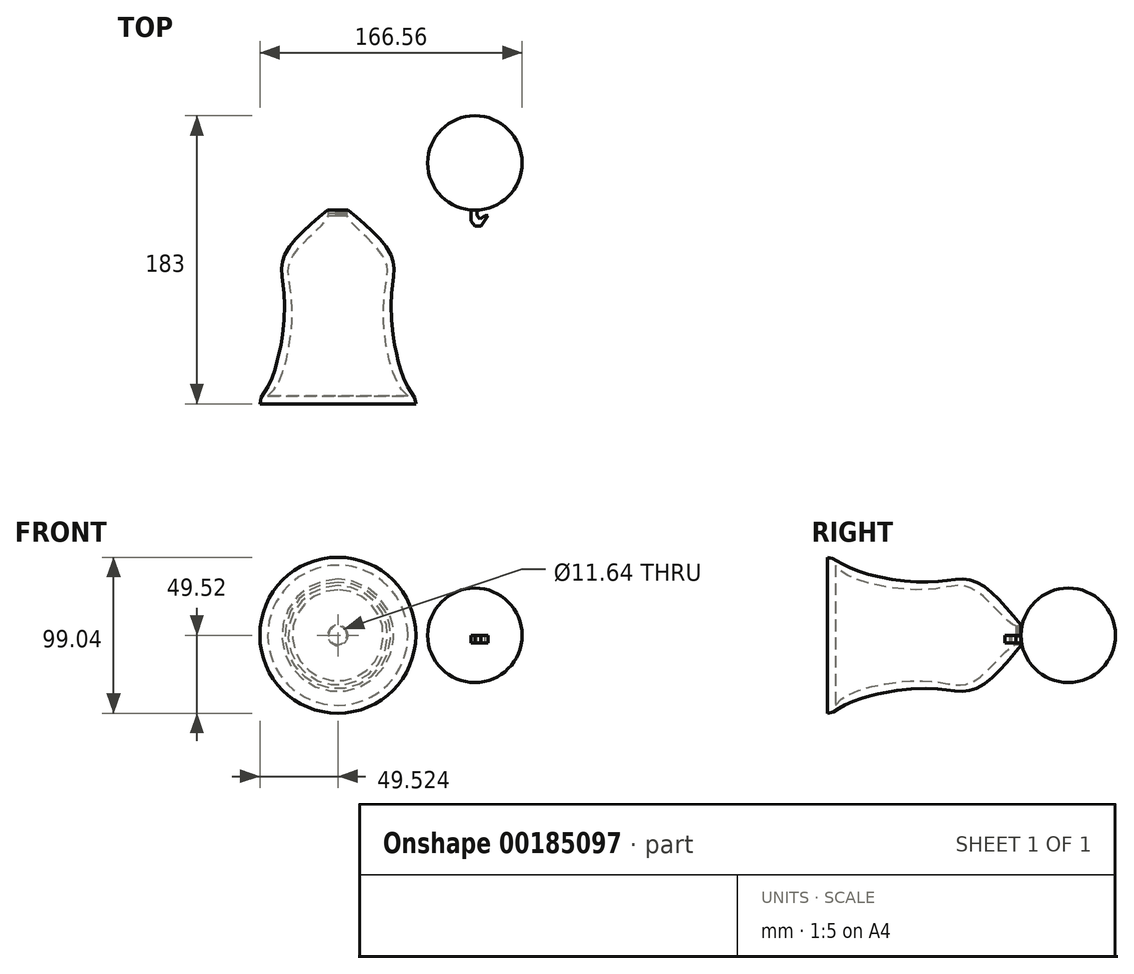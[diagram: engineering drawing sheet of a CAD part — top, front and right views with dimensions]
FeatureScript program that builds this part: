
annotation { "Feature Type Name" : "Feature", "Feature Type Description" : "" }
export const myFeature = defineFeature(function(context is Context, id is Id, definition is map)
    precondition{}
    {
        {
            var Q0;
            Q0=qCreatedBy(makeId("Top.planeOp"),FACE);
            var sketch = newSketch(context, id + "F0", { "sketchPlane" : qUnion([Q0])});
            skArc(sketch, "E0", {"start": v(0, 60) * mm, "mid": v(-30, 30) * mm, "end": v(0, 0) * mm});
            skLineSegment(sketch, "E1", {"start": v(0, 0) * mm, "end": v(0, 60) * mm});
            skSolve(sketch);
        }
        {
            var Q0;
            Q0=makeQuery(id+"F0.imprint","IMPRINT",FACE,{"disambiguationData":[TD([[makeQuery(id+"F0.imprint","IMPRINT",EDGE,{"derivedFrom":sQuery(id+"F0.wireOp",EDGE,"E0")}),1.0]])]});
            var Q1;
            Q1=sQuery(id+"F0.wireOp",EDGE,"E1");
            revolve(context, id + "F1", {"entities" : qUnion([Q0]), "axis" : qUnion([Q1]), "revolveType" : RevolveType.FULL});
        }
        {
            var Q0;
            Q0=qCreatedBy(makeId("Top.planeOp"),FACE);
            var sketch = newSketch(context, id + "F2", { "sketchPlane" : qUnion([Q0])});
            skFitSpline(sketch, "E2", {"points": [v(-93.48, 0) * mm, v(-121.53, -30.18) * mm, v(-120.8, -57.52) * mm, v(-130.25, -109.76) * mm, v(-136.56, -123) * mm], "startDerivative": vector(-134.32, -108.76) * mm, "endDerivative": vector(-0.75, -80.1) * mm});
            skLineSegment(sketch, "E3", {"start": v(-136.56, -123) * mm, "end": v(-87.04, -123) * mm});
            skFitSpline(sketch, "E4", {"points": [v(-93.48, 0) * mm, v(-93.48, -5) * mm, v(-116.53, -30.63) * mm, v(-116.1, -59.24) * mm, v(-131.51, -118) * mm], "startDerivative": vector(17.91, -48.79) * mm, "endDerivative": vector(-89.59, -57.64) * mm});
            skLineSegment(sketch, "E5", {"start": v(-131.51, -118) * mm, "end": v(-87.04, -118) * mm});
            skLineSegment(sketch, "E6", {"start": v(-92.86, -1.71) * mm, "end": v(-92.86, -3.4) * mm});
            skPoint(sketch, "E7.start.orphan", {"position": v(-83.12, 0) * mm});
            skLineSegment(sketch, "E8", {"start": v(-87.04, -118) * mm, "end": v(-87.04, -123) * mm});
            skSolve(sketch);
        }
        {
            var Q0;
            {var subQ4=sQuery(id+"F2.wireOp",EDGE,"E2");Q0=makeQuery(id+"F2.imprint","IMPRINT",FACE,{"disambiguationData":[TD([[makeQuery(id+"F2.imprint","IMPRINT",EDGE,{"derivedFrom":subQ4}),1.0]])]});}
            var Q1;
            Q1=sQuery(id+"F2.wireOp",EDGE,"E8");
            revolve(context, id + "F3", {"entities" : qUnion([Q0]), "axis" : qUnion([Q1]), "revolveType" : RevolveType.FULL});
        }
        {
            var Q0;
            Q0=qCreatedBy(makeId("Top.planeOp"),FACE);
            var sketch = newSketch(context, id + "F4", { "sketchPlane" : qUnion([Q0])});
            skLineSegment(sketch, "E9", {"start": v(-2.49, 0) * mm, "end": v(-2.49, -7) * mm});
            skLineSegment(sketch, "E10", {"start": v(-2.49, -7) * mm, "end": v(0, -10.13) * mm});
            skLineSegment(sketch, "E11", {"start": v(0, -10.13) * mm, "end": v(4, -10.13) * mm});
            skLineSegment(sketch, "E12", {"start": v(4, -10.13) * mm, "end": v(8.3, -3.39) * mm});
            skLineSegment(sketch, "E13", {"start": v(8.3, -3.39) * mm, "end": v(6.51, -3.39) * mm});
            skLineSegment(sketch, "E14", {"start": v(6.51, -3.39) * mm, "end": v(3.31, -5.79) * mm});
            skLineSegment(sketch, "E15", {"start": v(3.31, -5.79) * mm, "end": v(1.51, -3.39) * mm});
            skLineSegment(sketch, "E16", {"start": v(1.51, -3.39) * mm, "end": v(1.51, 0) * mm});
            skLineSegment(sketch, "E17", {"start": v(-2.49, 0) * mm, "end": v(1.51, 0) * mm});
            skSolve(sketch);
        }
        {
            var Q0;
            Q0=makeQuery(id+"F4.imprint","IMPRINT",FACE,{"disambiguationData":[TD([[makeQuery(id+"F4.imprint","IMPRINT",EDGE,{"derivedFrom":sQuery(id+"F4.wireOp",EDGE,"E9")}),1.0]])]});
            extrude(context, id + "F5", {"entities" : qUnion([Q0]), "oppositeDirection" : true, "depth" : 5 * mm});
        }
    });
